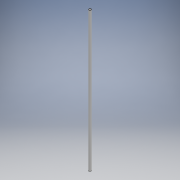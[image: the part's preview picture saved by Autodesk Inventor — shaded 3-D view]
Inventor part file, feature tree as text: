
AUTODESK INVENTOR PART (.ipt)
format: ipt  version: 2018 (Build 220112000, 112)  size: 96,768 bytes
history: native  units: mm
features: extrude x1, sketch x1
ambient origin geometry x8: Origin, YZ Plane, XZ Plane, XY Plane, X Axis, Y Axis, Z Axis, Center Point
bodies: Solid1 (feature_tree)
feature tree (2):
  extrude  "Extrusion1"  Depth=1884.0mm
  sketch  "Sketch1"  dims[d0=3.2mm d1=33.7mm d2=27.3mm d3=1884.0mm d4=0.0mm]
